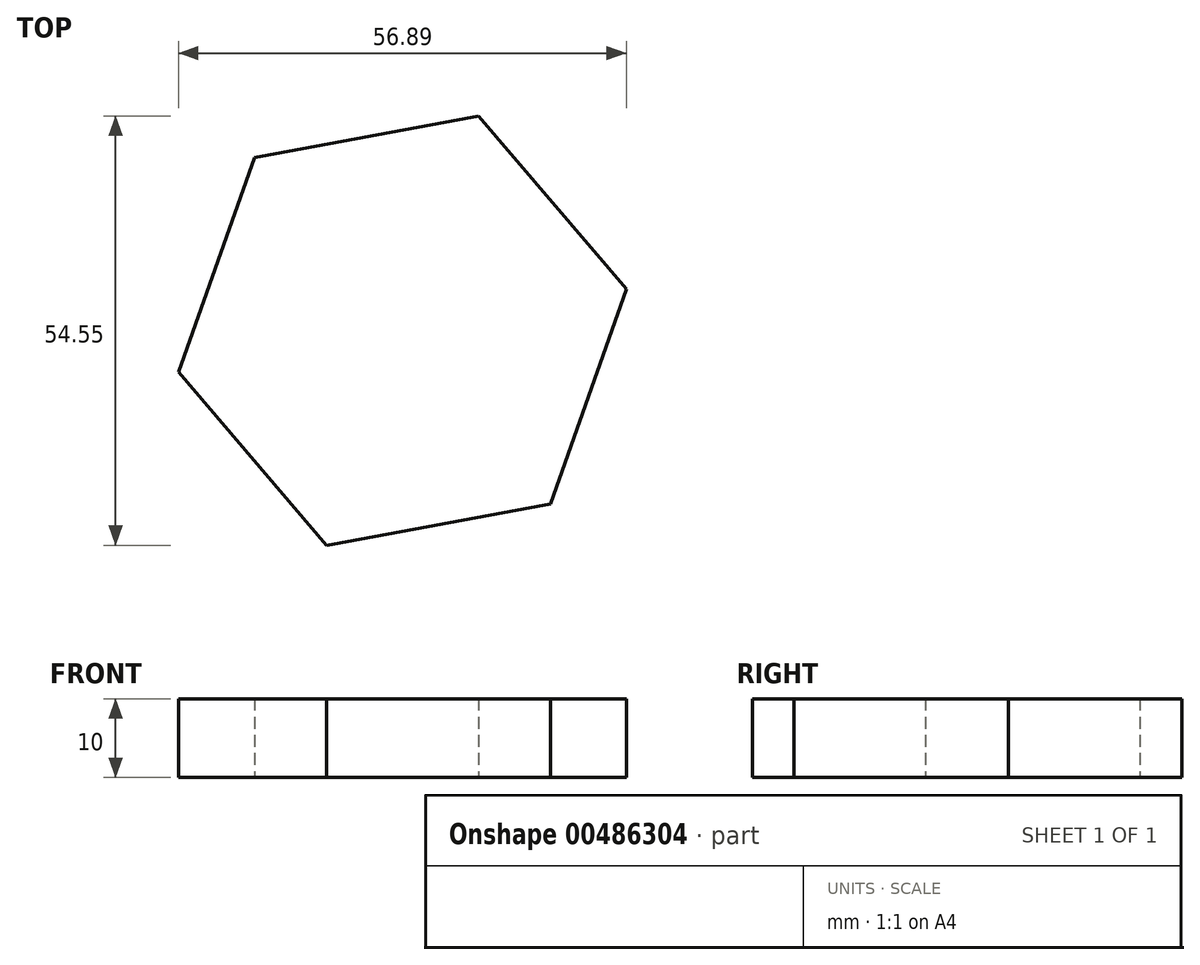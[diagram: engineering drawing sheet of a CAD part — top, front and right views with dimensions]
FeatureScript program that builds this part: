
annotation { "Feature Type Name" : "Feature", "Feature Type Description" : "" }
export const myFeature = defineFeature(function(context is Context, id is Id, definition is map)
    precondition{}
    {
        {
            var Q0;
            Q0=qCreatedBy(makeId("Top.planeOp"),FACE);
            var sketch = newSketch(context, id + "F0", { "sketchPlane" : qUnion([Q0])});
            skCircle(sketch, "E0.cCircle", {"center": v(-18.8, 37.21) * mm, "radius": 28.93 * mm, "construction": true});
            skLineSegment(sketch, "E0.0", {"start": v(0, 15.22) * mm, "end": v(-28.44, 9.94) * mm});
            skLineSegment(sketch, "E0.1", {"start": v(-28.44, 9.94) * mm, "end": v(-47.24, 31.93) * mm});
            skLineSegment(sketch, "E0.2", {"start": v(-47.24, 31.93) * mm, "end": v(-37.59, 59.2) * mm});
            skLineSegment(sketch, "E0.3", {"start": v(-37.59, 59.2) * mm, "end": v(-9.15, 64.49) * mm});
            skLineSegment(sketch, "E0.4", {"start": v(-9.15, 64.49) * mm, "end": v(9.65, 42.5) * mm});
            skLineSegment(sketch, "E0.5", {"start": v(9.65, 42.5) * mm, "end": v(0, 15.22) * mm});
            skSolve(sketch);
        }
        {
            var Q0;
            Q0=makeQuery(id+"F0.imprint","IMPRINT",FACE,{"disambiguationData":[TD([[makeQuery(id+"F0.imprint","IMPRINT",EDGE,{"derivedFrom":sQuery(id+"F0.wireOp",EDGE,"E0.0")}),-1.0]])]});
            extrude(context, id + "F1", {"entities" : qUnion([Q0]), "depth" : 10 * mm});
        }
    });
